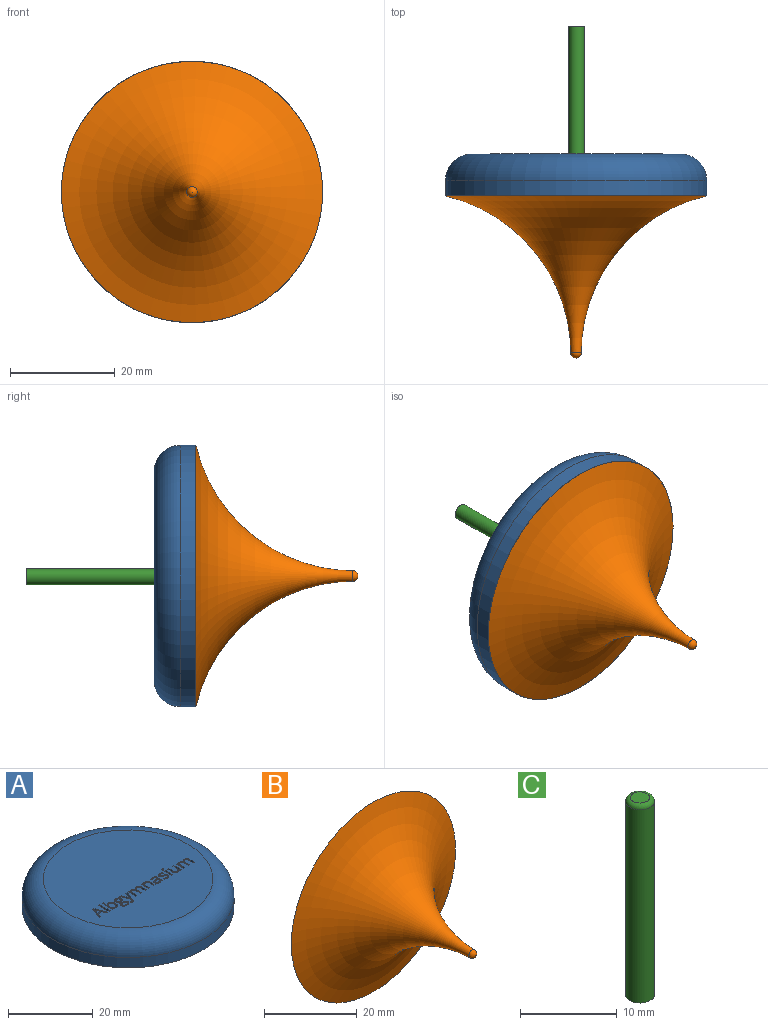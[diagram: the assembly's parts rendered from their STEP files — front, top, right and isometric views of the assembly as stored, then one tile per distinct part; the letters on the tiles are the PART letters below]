
ASSEMBLY  parts=3 mates=2
PART A: 276 faces, bbox 54.1x54.1x8 mm
  f0: plane 40x40mm, normal (0,0,1), area 1220.3mm2, adj f3,f4,f5,f6,f7,f22,f23,f24
  f1: cylinder r=25mm len=50mm, axis (0,0,-1), area 471.2mm2, adj f2,f3
  f2: plane 50x50mm, normal (0,0,-1), area 1963.5mm2, adj f1
  f3: torus R=20mm, axis (0,0,1), area 1144mm2, adj f0,f1
  f4: plane 3x0.38mm, normal (0,1,0), area 1.1mm2, adj f0,f5,f7,f8
  f5: plane 3.53x3mm, normal (-1,0,0), area 10.6mm2, adj f0,f4,f6,f8
  f6: plane 3x0.38mm, normal (0,-1,0), area 1.1mm2, adj f0,f5,f7,f8
  f7: plane 3.53x3mm, normal (1,0,0), area 10.6mm2, adj f0,f4,f6,f8
  f8: plane 3.53x0.38mm, normal (0,0,1), area 1.3mm2, adj f4,f5,f6,f7
  f9: extruded ~3x0.39mm, area 1.3mm2, adj f10,f52,f53,f272
  f10: extruded ~3x0.42mm, area 1.4mm2, adj f9,f11,f53,f272
  f11: extruded ~3x0.41mm, area 1.3mm2, adj f10,f12,f53,f272
  f12: extruded ~3x0.56mm, area 2.7mm2, adj f11,f13,f53,f272
  f13: extruded ~3x0.55mm, area 2.6mm2, adj f12,f52,f53,f272
  f14: extruded ~3x0.31mm, area 1.1mm2, adj f15,f50,f53,f54
  f15: extruded ~3x0.35mm, area 1.2mm2, adj f14,f16,f53,f54
  f16: extruded ~3x0.4mm, area 1.3mm2, adj f15,f17,f53,f54
  f17: plane 3x0.45mm, normal (0,1,0), area 1.4mm2, adj f16,f18,f53,f54
  f18: extruded ~3x0.47mm, area 1.4mm2, adj f17,f19,f53,f54
  f19: extruded ~3x0.28mm, area 1mm2, adj f18,f20,f53,f54
  f20: extruded ~3x0.38mm, area 1.4mm2, adj f19,f21,f53,f54
  f21: extruded ~3x0.7mm, area 2.2mm2, adj f20,f50,f53,f54
  f22: plane 3x0.24mm, normal (-1,0,0), area 0.7mm2, adj f0,f23,f51,f53
  f23: plane 3x0.86mm, normal (0,-1,0), area 2.6mm2, adj f0,f22,f24,f53
  f24: extruded ~3x0.35mm, area 1.1mm2, adj f0,f23,f25,f53
  f25: extruded ~3x0.69mm, area 2.2mm2, adj f0,f24,f26,f53
  f26: extruded ~3x0.63mm, area 2.1mm2, adj f0,f25,f27,f53
  f27: extruded ~3x0.44mm, area 1.4mm2, adj f0,f26,f28,f53
  f28: extruded ~3x0.31mm, area 1.3mm2, adj f0,f27,f29,f53
  f29: extruded ~3x0.23mm, area 0.9mm2, adj f0,f28,f30,f53
  f30: extruded ~3x0.24mm, area 0.8mm2, adj f0,f29,f31,f53
  f31: extruded ~3x0.21mm, area 0.7mm2, adj f0,f30,f32,f53
  f32: extruded ~3x0.16mm, area 0.6mm2, adj f0,f31,f33,f53
  f33: extruded ~3x0.41mm, area 1.4mm2, adj f0,f32,f34,f53
  f34: extruded ~3x0.39mm, area 1.3mm2, adj f0,f33,f35,f53
  f35: extruded ~3x0.51mm, area 1.8mm2, adj f0,f34,f36,f53
  f36: extruded ~3x0.75mm, area 2.4mm2, adj f0,f35,f37,f53
  f37: extruded ~3x0.97mm, area 3mm2, adj f0,f36,f38,f53
  f38: extruded ~3x0.63mm, area 2.2mm2, adj f0,f37,f39,f53
  f39: extruded ~3x0.5mm, area 1.7mm2, adj f0,f38,f40,f53
  f40: extruded ~3x0.62mm, area 2mm2, adj f0,f39,f41,f53
  f41: plane 3x0.44mm, normal (0,-1,0), area 1.3mm2, adj f0,f40,f42,f53
  f42: extruded ~3x0.29mm, area 0.9mm2, adj f0,f41,f43,f53
  f43: extruded ~3x0.15mm, area 0.5mm2, adj f0,f42,f44,f53
  f44: extruded ~3x0.32mm, area 1.3mm2, adj f0,f43,f45,f53
  f45: extruded ~3x0.21mm, area 0.6mm2, adj f0,f44,f46,f53
  f46: extruded ~3x0.69mm, area 2.2mm2, adj f0,f45,f47,f53
  f47: extruded ~3x0.58mm, area 2mm2, adj f0,f46,f48,f53
  f48: extruded ~3x0.29mm, area 0.9mm2, adj f0,f47,f49,f53
  f49: extruded ~3x0.21mm, area 0.7mm2, adj f0,f48,f51,f53
  f50: extruded ~3x0.49mm, area 1.5mm2, adj f14,f21,f53,f54
  f51: plane 3x0.46mm, normal (-0.12,0.99,0), area 1.4mm2, adj f0,f22,f49,f53
  f52: extruded ~3x0.41mm, area 1.3mm2, adj f9,f13,f53,f272
  f53: plane 3.65x2.35mm, normal (0,0,1), area 3.5mm2, adj f9,f10,f11,f12,f13,f14,f15,f16
  f54: plane 1.59x0.89mm, normal (0,0,1), area 1.2mm2, adj f14,f15,f16,f17,f18,f19,f20,f21
  f55: extruded ~3x0.55mm, area 1.8mm2, adj f56,f81,f82,f273
  f56: extruded ~3x0.35mm, area 1.1mm2, adj f55,f57,f82,f273
  f57: extruded ~3x0.31mm, area 1mm2, adj f56,f58,f82,f273
  f58: extruded ~3x0.38mm, area 1.4mm2, adj f57,f59,f82,f273
  f59: extruded ~3x0.65mm, area 2mm2, adj f58,f60,f82,f273
  f60: plane 3x0.38mm, normal (-0.04,1,0), area 1.1mm2, adj f59,f61,f82,f273
  f61: plane 3x0.22mm, normal (1,0,0), area 0.7mm2, adj f60,f81,f82,f273
  f62: plane 3x0.35mm, normal (0.98,0.21,0), area 1.1mm2, adj f0,f63,f80,f82
  f63: plane 3x0.28mm, normal (0,1,0), area 0.8mm2, adj f0,f62,f64,f82
  f64: plane 3x1.7mm, normal (-1,0,0), area 5.1mm2, adj f0,f63,f65,f82
  f65: extruded ~3x0.63mm, area 2.1mm2, adj f0,f64,f66,f82
  f66: extruded ~3x0.66mm, area 2.1mm2, adj f0,f65,f67,f82
  f67: extruded ~3x0.44mm, area 1.3mm2, adj f0,f66,f68,f82
  f68: extruded ~3x0.4mm, area 1.3mm2, adj f0,f67,f69,f82
  f69: plane 3x0.29mm, normal (0.93,0.37,0), area 0.9mm2, adj f0,f68,f70,f82
  f70: extruded ~3x0.7mm, area 2.2mm2, adj f0,f69,f71,f82
  f71: extruded ~3x0.4mm, area 1.3mm2, adj f0,f70,f72,f82
  f72: extruded ~3x0.43mm, area 1.4mm2, adj f0,f71,f73,f82
  f73: plane 3x0.15mm, normal (1,0,0), area 0.5mm2, adj f0,f72,f74,f82
  f74: plane 3x0.42mm, normal (0.03,-1,0), area 1.3mm2, adj f0,f73,f75,f82
  f75: extruded ~3x1.2mm, area 4.9mm2, adj f0,f74,f76,f82
  f76: extruded ~3x0.54mm, area 1.8mm2, adj f0,f75,f77,f82
  f77: extruded ~3x0.58mm, area 1.9mm2, adj f0,f76,f78,f82
  f78: extruded ~3x0.46mm, area 1.4mm2, adj f0,f77,f79,f82
  f79: extruded ~3x0.37mm, area 1.5mm2, adj f0,f78,f80,f82
  f80: plane 3x0.02mm, normal (0,1,0), area 0.1mm2, adj f0,f62,f79,f82
  f81: extruded ~3x0.54mm, area 1.8mm2, adj f55,f61,f82,f273
  f82: plane 2.57x1.99mm, normal (0,0,1), area 2.4mm2, adj f55,f56,f57,f58,f59,f60,f61,f62
  f83: extruded ~3x0.56mm, area 1.9mm2, adj f84,f105,f106,f274
  f84: extruded ~3x0.53mm, area 1.8mm2, adj f83,f85,f106,f274
  f85: extruded ~3x0.72mm, area 2.3mm2, adj f84,f86,f106,f274
  f86: extruded ~3x0.73mm, area 2.3mm2, adj f85,f87,f106,f274
  f87: extruded ~3x0.52mm, area 1.8mm2, adj f86,f88,f106,f274
  f88: extruded ~3x0.56mm, area 1.9mm2, adj f87,f89,f106,f274
  f89: extruded ~3x0.75mm, area 2.3mm2, adj f88,f105,f106,f274
  f90: extruded ~3x0.76mm, area 2.6mm2, adj f0,f91,f104,f106
  f91: extruded ~3x0.78mm, area 2.7mm2, adj f0,f90,f92,f106
  f92: plane 3x0.02mm, normal (0,-1,0), area 0.1mm2, adj f0,f91,f93,f106
  f93: extruded ~3x0.52mm, area 1.6mm2, adj f0,f92,f94,f106
  f94: plane 3x0.86mm, normal (-1,0,0), area 2.6mm2, adj f0,f93,f95,f106
  f95: plane 3x0.38mm, normal (0,-1,0), area 1.1mm2, adj f0,f94,f96,f106
  f96: plane 3.53x3mm, normal (1,0,0), area 10.6mm2, adj f0,f95,f97,f106
  f97: plane 3x0.27mm, normal (0,1,0), area 0.8mm2, adj f0,f96,f98,f106
  f98: plane 3x0.32mm, normal (-0.97,0.24,0), area 1mm2, adj f0,f97,f99,f106
  f99: plane 3x0.03mm, normal (0,1,0), area 0.1mm2, adj f0,f98,f100,f106
  f100: extruded ~3x0.34mm, area 1.3mm2, adj f0,f99,f101,f106
  f101: extruded ~3x0.44mm, area 1.4mm2, adj f0,f100,f102,f106
  f102: extruded ~3x0.76mm, area 2.6mm2, adj f0,f101,f103,f106
  f103: extruded ~3x0.95mm, area 3mm2, adj f0,f102,f104,f106
  f104: extruded ~3x0.95mm, area 3mm2, adj f0,f90,f103,f106
  f105: extruded ~3x0.75mm, area 2.3mm2, adj f83,f89,f106,f274
  f106: plane 3.58x2.19mm, normal (0,0,1), area 3mm2, adj f83,f84,f85,f86,f87,f88,f89,f90
  f107: plane 3x1.03mm, normal (0.94,0.35,0), area 3.3mm2, adj f108,f119,f120,f275
  f108: plane 3x1.07mm, normal (0,-1,0), area 3.2mm2, adj f107,f109,f120,f275
  f109: plane 3x1.03mm, normal (-0.94,0.35,0), area 3.3mm2, adj f108,f110,f120,f275
  f110: extruded ~3x0.48mm, area 1.5mm2, adj f109,f119,f120,f275
  f111: plane 3x1.06mm, normal (0.93,0.36,0), area 3.4mm2, adj f0,f112,f118,f120
  f112: plane 3x0.4mm, normal (0,1,0), area 1.2mm2, adj f0,f111,f113,f120
  f113: plane 3.33x3mm, normal (-0.93,-0.36,0), area 10.7mm2, adj f0,f112,f114,f120
  f114: plane 3x0.32mm, normal (0,-1,0), area 1mm2, adj f0,f113,f115,f120
  f115: plane 3.33x3mm, normal (0.93,-0.37,0), area 10.7mm2, adj f0,f114,f116,f120
  f116: plane 3x0.39mm, normal (0,1,0), area 1.2mm2, adj f0,f115,f117,f120
  f117: plane 3x1.06mm, normal (-0.93,0.36,0), area 3.4mm2, adj f0,f116,f118,f120
  f118: plane 3x1.33mm, normal (0,1,0), area 4mm2, adj f0,f111,f117,f120
  f119: extruded ~3x0.48mm, area 1.5mm2, adj f107,f110,f120,f275
  f120: plane 3.33x2.94mm, normal (0,0,1), area 2.8mm2, adj f107,f108,f109,f110,f111,f112,f113,f114
  f121: plane 3x1.62mm, normal (1,0,0), area 4.9mm2, adj f0,f122,f148,f149
  f122: plane 3x0.38mm, normal (0,1,0), area 1.1mm2, adj f0,f121,f123,f149
  f123: plane 3x1.62mm, normal (-1,0,0), area 4.9mm2, adj f0,f122,f124,f149
  f124: extruded ~3x0.69mm, area 2.2mm2, adj f0,f123,f125,f149
  f125: extruded ~3x0.63mm, area 2.1mm2, adj f0,f124,f126,f149
  f126: extruded ~3x0.48mm, area 1.5mm2, adj f0,f125,f127,f149
  f127: extruded ~3x0.32mm, area 1.4mm2, adj f0,f126,f128,f149
  f128: plane 3x0.02mm, normal (0,-1,0), area 0.1mm2, adj f0,f127,f129,f149
  f129: extruded ~3x0.76mm, area 2.8mm2, adj f0,f128,f130,f149
  f130: extruded ~3x0.43mm, area 1.4mm2, adj f0,f129,f131,f149
  f131: extruded ~3x0.3mm, area 1.3mm2, adj f0,f130,f132,f149
  f132: plane 3x0.02mm, normal (0,-1,0), area 0.1mm2, adj f0,f131,f133,f149
  f133: plane 3x0.34mm, normal (-0.98,-0.18,0), area 1mm2, adj f0,f132,f134,f149
  f134: plane 3x0.31mm, normal (0,-1,0), area 0.9mm2, adj f0,f133,f135,f149
  f135: plane 3x2.49mm, normal (1,0,0), area 7.5mm2, adj f0,f134,f136,f149
  f136: plane 3x0.38mm, normal (0,1,0), area 1.1mm2, adj f0,f135,f137,f149
  f137: plane 3x1.31mm, normal (-1,0,0), area 3.9mm2, adj f0,f136,f138,f149
  f138: extruded ~3x0.7mm, area 2.2mm2, adj f0,f137,f139,f149
  f139: extruded ~3x0.52mm, area 1.7mm2, adj f0,f138,f140,f149
  f140: extruded ~3x0.4mm, area 1.3mm2, adj f0,f139,f141,f149
  f141: extruded ~3x0.45mm, area 1.4mm2, adj f0,f140,f142,f149
  f142: plane 3x1.62mm, normal (1,0,0), area 4.9mm2, adj f0,f141,f143,f149
  f143: plane 3x0.38mm, normal (0,1,0), area 1.1mm2, adj f0,f142,f144,f149
  f144: plane 3x1.39mm, normal (-1,0,0), area 4.2mm2, adj f0,f143,f145,f149
  f145: extruded ~3x0.62mm, area 2mm2, adj f0,f144,f146,f149
  f146: extruded ~3x0.52mm, area 1.7mm2, adj f0,f145,f147,f149
  f147: extruded ~3x0.4mm, area 1.3mm2, adj f0,f146,f148,f149
  f148: extruded ~3x0.45mm, area 1.4mm2, adj f0,f121,f147,f149
  f149: plane 3.55x2.53mm, normal (0,0,1), area 3.5mm2, adj f121,f122,f123,f124,f125,f126,f127,f128
  f150: plane 3x1.61mm, normal (-1,0,0), area 4.8mm2, adj f0,f151,f166,f167
  f151: plane 3x0.38mm, normal (0,-1,0), area 1.1mm2, adj f0,f150,f152,f167
  f152: plane 3x1.63mm, normal (1,0,0), area 4.9mm2, adj f0,f151,f153,f167
  f153: extruded ~3x0.69mm, area 2.2mm2, adj f0,f152,f154,f167
  f154: extruded ~3x0.68mm, area 2.2mm2, adj f0,f153,f155,f167
  f155: extruded ~3x0.47mm, area 1.4mm2, adj f0,f154,f156,f167
  f156: extruded ~3x0.32mm, area 1.3mm2, adj f0,f155,f157,f167
  f157: plane 3x0.02mm, normal (0,1,0), area 0.1mm2, adj f0,f156,f158,f167
  f158: plane 3x0.33mm, normal (0.99,0.16,0), area 1mm2, adj f0,f157,f159,f167
  f159: plane 3x0.31mm, normal (0,1,0), area 0.9mm2, adj f0,f158,f160,f167
  f160: plane 3x2.49mm, normal (-1,0,0), area 7.5mm2, adj f0,f159,f161,f167
  f161: plane 3x0.38mm, normal (0,-1,0), area 1.1mm2, adj f0,f160,f162,f167
  f162: plane 3x1.31mm, normal (1,0,0), area 3.9mm2, adj f0,f161,f163,f167
  f163: extruded ~3x0.7mm, area 2.2mm2, adj f0,f162,f164,f167
  f164: extruded ~3x0.57mm, area 1.9mm2, adj f0,f163,f165,f167
  f165: extruded ~3x0.43mm, area 1.4mm2, adj f0,f164,f166,f167
  f166: extruded ~3x0.45mm, area 1.5mm2, adj f0,f150,f165,f167
  f167: plane 2.53x2.08mm, normal (0,0,1), area 2.3mm2, adj f150,f151,f152,f153,f154,f155,f156,f157
  f168: extruded ~3x0.19mm, area 0.6mm2, adj f0,f169,f175,f176
  f169: extruded ~3x0.19mm, area 0.6mm2, adj f0,f168,f170,f176
  f170: extruded ~3x0.16mm, area 0.5mm2, adj f0,f169,f171,f176
  f171: extruded ~3x0.16mm, area 0.5mm2, adj f0,f170,f172,f176
  f172: extruded ~3x0.19mm, area 0.6mm2, adj f0,f171,f173,f176
  f173: extruded ~3x0.19mm, area 0.6mm2, adj f0,f172,f174,f176
  f174: extruded ~3x0.16mm, area 0.5mm2, adj f0,f173,f175,f176
  f175: extruded ~3x0.16mm, area 0.5mm2, adj f0,f168,f174,f176
  f176: plane 0.5x0.45mm, normal (0,0,1), area 0.2mm2, adj f168,f169,f170,f171,f172,f173,f174,f175
  f177: plane 3x0.38mm, normal (0,1,0), area 1.1mm2, adj f0,f178,f180,f181
  f178: plane 3x2.49mm, normal (-1,0,0), area 7.5mm2, adj f0,f177,f179,f181
  f179: plane 3x0.38mm, normal (0,-1,0), area 1.1mm2, adj f0,f178,f180,f181
  f180: plane 3x2.49mm, normal (1,0,0), area 7.5mm2, adj f0,f177,f179,f181
  f181: plane 2.49x0.38mm, normal (0,0,1), area 0.9mm2, adj f177,f178,f179,f180
  f182: extruded ~3x0.54mm, area 1.9mm2, adj f0,f183,f206,f207
  f183: extruded ~3x0.41mm, area 1.4mm2, adj f0,f182,f184,f207
  f184: extruded ~3x0.6mm, area 2.1mm2, adj f0,f183,f185,f207
  f185: extruded ~3x0.44mm, area 1.4mm2, adj f0,f184,f186,f207
  f186: extruded ~3x0.16mm, area 0.6mm2, adj f0,f185,f187,f207
  f187: extruded ~3x0.17mm, area 0.5mm2, adj f0,f186,f188,f207
  f188: extruded ~3x0.23mm, area 0.8mm2, adj f0,f187,f189,f207
  f189: extruded ~3x0.4mm, area 1.3mm2, adj f0,f188,f190,f207
  f190: extruded ~3x0.68mm, area 2.1mm2, adj f0,f189,f191,f207
  f191: plane 3x0.31mm, normal (-0.92,0.4,0), area 1mm2, adj f0,f190,f192,f207
  f192: extruded ~3x0.79mm, area 2.4mm2, adj f0,f191,f193,f207
  f193: extruded ~3x0.68mm, area 2.1mm2, adj f0,f192,f194,f207
  f194: extruded ~3x0.48mm, area 1.7mm2, adj f0,f193,f195,f207
  f195: extruded ~3x0.29mm, area 0.9mm2, adj f0,f194,f196,f207
  f196: extruded ~3x0.22mm, area 0.9mm2, adj f0,f195,f197,f207
  f197: extruded ~3x0.49mm, area 1.6mm2, adj f0,f196,f198,f207
  f198: extruded ~3x0.49mm, area 1.7mm2, adj f0,f197,f199,f207
  f199: extruded ~3x0.25mm, area 0.9mm2, adj f0,f198,f200,f207
  f200: extruded ~3x0.29mm, area 1mm2, adj f0,f199,f201,f207
  f201: extruded ~3x0.45mm, area 1.4mm2, adj f0,f200,f202,f207
  f202: extruded ~3x0.4mm, area 1.2mm2, adj f0,f201,f203,f207
  f203: extruded ~3x0.38mm, area 1.2mm2, adj f0,f202,f204,f207
  f204: plane 3x0.35mm, normal (1,0,0), area 1mm2, adj f0,f203,f205,f207
  f205: extruded ~3x0.77mm, area 2.4mm2, adj f0,f204,f206,f207
  f206: extruded ~3x0.73mm, area 2.3mm2, adj f0,f182,f205,f207
  f207: plane 2.58x1.76mm, normal (0,0,1), area 1.9mm2, adj f182,f183,f184,f185,f186,f187,f188,f189
  f208: plane 3x1.61mm, normal (1,0,0), area 4.8mm2, adj f0,f209,f224,f225
  f209: plane 3x0.38mm, normal (0,1,0), area 1.1mm2, adj f0,f208,f210,f225
  f210: plane 3x1.62mm, normal (-1,0,0), area 4.9mm2, adj f0,f209,f211,f225
  f211: extruded ~3x0.69mm, area 2.3mm2, adj f0,f210,f212,f225
  f212: extruded ~3x0.68mm, area 2.2mm2, adj f0,f211,f213,f225
  f213: extruded ~3x0.47mm, area 1.4mm2, adj f0,f212,f214,f225
  f214: extruded ~3x0.33mm, area 1.3mm2, adj f0,f213,f215,f225
  f215: plane 3x0.02mm, normal (0,-1,0), area 0.1mm2, adj f0,f214,f216,f225
  f216: plane 3x0.34mm, normal (-0.98,-0.18,0), area 1mm2, adj f0,f215,f217,f225
  f217: plane 3x0.31mm, normal (0,-1,0), area 0.9mm2, adj f0,f216,f218,f225
  f218: plane 3x2.49mm, normal (1,0,0), area 7.5mm2, adj f0,f217,f219,f225
  f219: plane 3x0.38mm, normal (0,1,0), area 1.1mm2, adj f0,f218,f220,f225
  f220: plane 3x1.31mm, normal (-1,0,0), area 3.9mm2, adj f0,f219,f221,f225
  f221: extruded ~3x0.7mm, area 2.2mm2, adj f0,f220,f222,f225
  f222: extruded ~3x0.57mm, area 1.9mm2, adj f0,f221,f223,f225
  f223: extruded ~3x0.43mm, area 1.4mm2, adj f0,f222,f224,f225
  f224: extruded ~3x0.45mm, area 1.5mm2, adj f0,f208,f223,f225
  f225: plane 2.53x2.08mm, normal (0,0,1), area 2.2mm2, adj f208,f209,f210,f211,f212,f213,f214,f215
  f226: plane 3x1.62mm, normal (1,0,0), area 4.9mm2, adj f0,f227,f253,f254
  f227: plane 3x0.38mm, normal (0,1,0), area 1.1mm2, adj f0,f226,f228,f254
  f228: plane 3x1.62mm, normal (-1,0,0), area 4.9mm2, adj f0,f227,f229,f254
  f229: extruded ~3x0.69mm, area 2.2mm2, adj f0,f228,f230,f254
  f230: extruded ~3x0.63mm, area 2.1mm2, adj f0,f229,f231,f254
  f231: extruded ~3x0.48mm, area 1.5mm2, adj f0,f230,f232,f254
  f232: extruded ~3x0.32mm, area 1.4mm2, adj f0,f231,f233,f254
  f233: plane 3x0.02mm, normal (0,-1,0), area 0.1mm2, adj f0,f232,f234,f254
  f234: extruded ~3x0.76mm, area 2.8mm2, adj f0,f233,f235,f254
  f235: extruded ~3x0.43mm, area 1.4mm2, adj f0,f234,f236,f254
  f236: extruded ~3x0.3mm, area 1.3mm2, adj f0,f235,f237,f254
  f237: plane 3x0.02mm, normal (0,-1,0), area 0.1mm2, adj f0,f236,f238,f254
  f238: plane 3x0.34mm, normal (-0.98,-0.18,0), area 1mm2, adj f0,f237,f239,f254
  f239: plane 3x0.31mm, normal (0,-1,0), area 0.9mm2, adj f0,f238,f240,f254
  f240: plane 3x2.49mm, normal (1,0,0), area 7.5mm2, adj f0,f239,f241,f254
  f241: plane 3x0.38mm, normal (0,1,0), area 1.1mm2, adj f0,f240,f242,f254
  f242: plane 3x1.31mm, normal (-1,0,0), area 3.9mm2, adj f0,f241,f243,f254
  f243: extruded ~3x0.7mm, area 2.2mm2, adj f0,f242,f244,f254
  f244: extruded ~3x0.52mm, area 1.7mm2, adj f0,f243,f245,f254
  f245: extruded ~3x0.4mm, area 1.3mm2, adj f0,f244,f246,f254
  f246: extruded ~3x0.45mm, area 1.4mm2, adj f0,f245,f247,f254
  f247: plane 3x1.62mm, normal (1,0,0), area 4.9mm2, adj f0,f246,f248,f254
  f248: plane 3x0.38mm, normal (0,1,0), area 1.1mm2, adj f0,f247,f249,f254
  f249: plane 3x1.39mm, normal (-1,0,0), area 4.2mm2, adj f0,f248,f250,f254
  f250: extruded ~3x0.62mm, area 2mm2, adj f0,f249,f251,f254
  f251: extruded ~3x0.52mm, area 1.7mm2, adj f0,f250,f252,f254
  f252: extruded ~3x0.4mm, area 1.3mm2, adj f0,f251,f253,f254
  f253: extruded ~3x0.45mm, area 1.4mm2, adj f0,f226,f252,f254
  f254: plane 3.55x2.53mm, normal (0,0,1), area 3.5mm2, adj f226,f227,f228,f229,f230,f231,f232,f233
  f255: plane 3x0.4mm, normal (0,-1,0), area 1.2mm2, adj f0,f256,f270,f271
  f256: plane 3x2.5mm, normal (0.93,0.37,0), area 8.1mm2, adj f0,f255,f257,f271
  f257: plane 3x0.35mm, normal (0.93,-0.37,0), area 1.1mm2, adj f0,f256,f258,f271
  f258: extruded ~3x0.55mm, area 2.3mm2, adj f0,f257,f259,f271
  f259: extruded ~3x0.28mm, area 0.8mm2, adj f0,f258,f260,f271
  f260: plane 3x0.3mm, normal (1,0,0), area 0.9mm2, adj f0,f259,f261,f271
  f261: extruded ~3x0.34mm, area 1mm2, adj f0,f260,f262,f271
  f262: extruded ~3x0.52mm, area 1.7mm2, adj f0,f261,f263,f271
  f263: extruded ~3x0.6mm, area 2.1mm2, adj f0,f262,f264,f271
  f264: plane 3x2.83mm, normal (-0.94,0.35,0), area 9.1mm2, adj f0,f263,f265,f271
  f265: plane 3x0.4mm, normal (0,-1,0), area 1.2mm2, adj f0,f264,f266,f271
  f266: extruded ~3x1.72mm, area 5.5mm2, adj f0,f265,f267,f271
  f267: extruded ~3x0.4mm, area 1.2mm2, adj f0,f266,f268,f271
  f268: plane 3x0.02mm, normal (0,-1,0), area 0.1mm2, adj f0,f267,f269,f271
  f269: extruded ~3x0.7mm, area 2.2mm2, adj f0,f268,f270,f271
  f270: plane 3x1.42mm, normal (-0.93,-0.36,0), area 4.6mm2, adj f0,f255,f269,f271
  f271: plane 3.6x2.33mm, normal (0,0,1), area 2.4mm2, adj f255,f256,f257,f258,f259,f260,f261,f262
  f272: plane 1.11x1.1mm, normal (0,0,1), area 1mm2, adj f9,f10,f11,f12,f13,f52
  f273: plane 1.22x0.96mm, normal (0,0,1), area 0.9mm2, adj f55,f56,f57,f58,f59,f60,f61,f81
  f274: plane 1.94x1.42mm, normal (0,0,1), area 2.3mm2, adj f83,f84,f85,f86,f87,f88,f89,f105
  f275: plane 1.51x1.07mm, normal (0,0,1), area 0.8mm2, adj f107,f108,f109,f110,f119
PART B: 3 faces, bbox 69.1x31.8x69.1 mm
  f0: plane 50x50mm, normal (0,1,0), area 1963.5mm2, adj f1
  f1: torus R=31.92mm, axis (0,1,0), area 2485.7mm2, adj f0,f2
  f2: torus R=0.01mm, axis (0,1,0), area 6.3mm2, adj f1
PART C: 4 faces, bbox 3.2x3.2x25 mm
  f0: cylinder r=1.5mm len=24.5mm, axis (0,0,-1), area 230.9mm2, adj f2,f3
  f1: plane 2x2mm, normal (0,0,1), area 3.1mm2, adj f3
  f2: plane 3x3mm, normal (0,0,-1), area 7.1mm2, adj f0
  f3: torus R=1mm, axis (0,0,1), area 6.5mm2, adj f0,f1
PLACE A rot(axis=(-1,0,0),90deg) t=(3.86,19.73,0)mm
PLACE B at identity
PLACE C rot(axis=(1,0,0),90deg) t=(3.92,52.23,-0.15)mm
MATE fastened C.f0 <-> A.f0  axis (0,1,0) through (3.92,27.73,-0.15)mm
MATE fastened A.f1 <-> B.f2  axis (0,-1,0) through (3.86,19.73,0)mm
